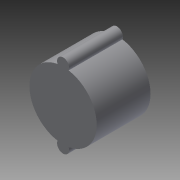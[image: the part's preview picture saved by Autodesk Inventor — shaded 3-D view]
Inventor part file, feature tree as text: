
AUTODESK INVENTOR PART (.ipt)
format: ipt  version: 2015 (Build 190159000, 159)  size: 82,432 bytes
history: native  units: mm
features: extrude x1, sketch x1
ambient origin geometry x8: Origin, YZ Plane, XZ Plane, XY Plane, X Axis, Y Axis, Z Axis, Center Point
bodies: Solid1 (feature_tree)
feature tree (2):
  extrude  "Extrusion1"  Depth=10.16mm
  sketch  "Sketch1"  dims[d0=12.7mm d1=2.286mm d2=2.286mm d3=6.731mm d4=6.731mm d5=13.462mm d6=10.16mm d7=0.0mm]
